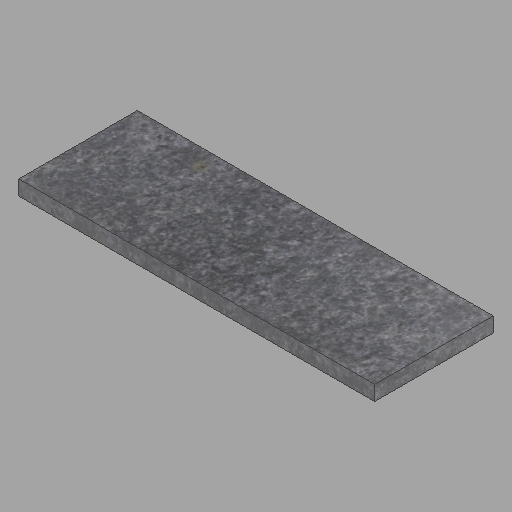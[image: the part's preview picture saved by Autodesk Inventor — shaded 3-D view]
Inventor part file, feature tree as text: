
AUTODESK INVENTOR PART (.ipt)
format: ipt  version: 2023 (Build 270158000, 158)  size: 208,384 bytes
history: native  units: in
note: dims shown in document units (in); Inventor stores cm internally (conversion verified against a paired STEP export)
features: other x1, extrude x1, sketch x1
ambient origin geometry x8: Origin, YZ Plane, XZ Plane, XY Plane, X Axis, Y Axis, Z Axis, Center Point
bodies: Solid1 (feature_tree)
feature tree (3):
  other  "2x16x48-5"
  extrude  "Extrusion1"  Depth=16.0in
  sketch  "Sketch1"  dims[d0=2.0in d1=16.0in d2=48.0in d3=0.0in]
